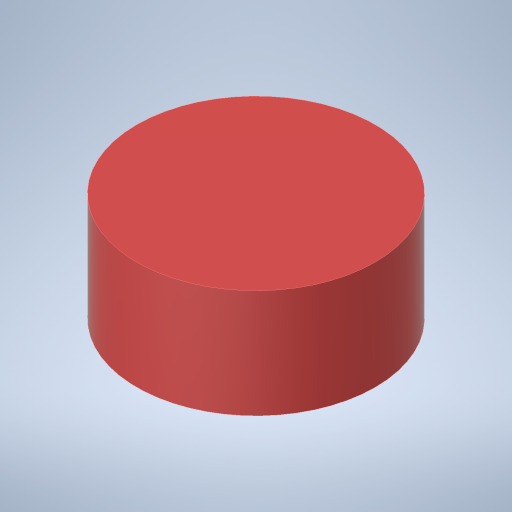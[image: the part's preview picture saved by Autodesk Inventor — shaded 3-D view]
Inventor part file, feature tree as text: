
AUTODESK INVENTOR PART (.ipt)
format: ipt  version: 2023.4 (Build 274418000, 418)  size: 196,096 bytes
history: native  units: in
note: dims shown in document units (in); Inventor stores cm internally (conversion verified against a paired STEP export)
features: extrude x1, sketch x1
ambient origin geometry x8: Origin, YZ Plane, XZ Plane, XY Plane, X Axis, Y Axis, Z Axis, Center Point
bodies: Solid1 (feature_tree)
feature tree (2):
  extrude  "Extrusion1"  Depth=0.3125in TaperAngle=0.0deg
  sketch  "Sketch1"  dims[d0=0.6875in d1=0.3125in d2=0.0in]
